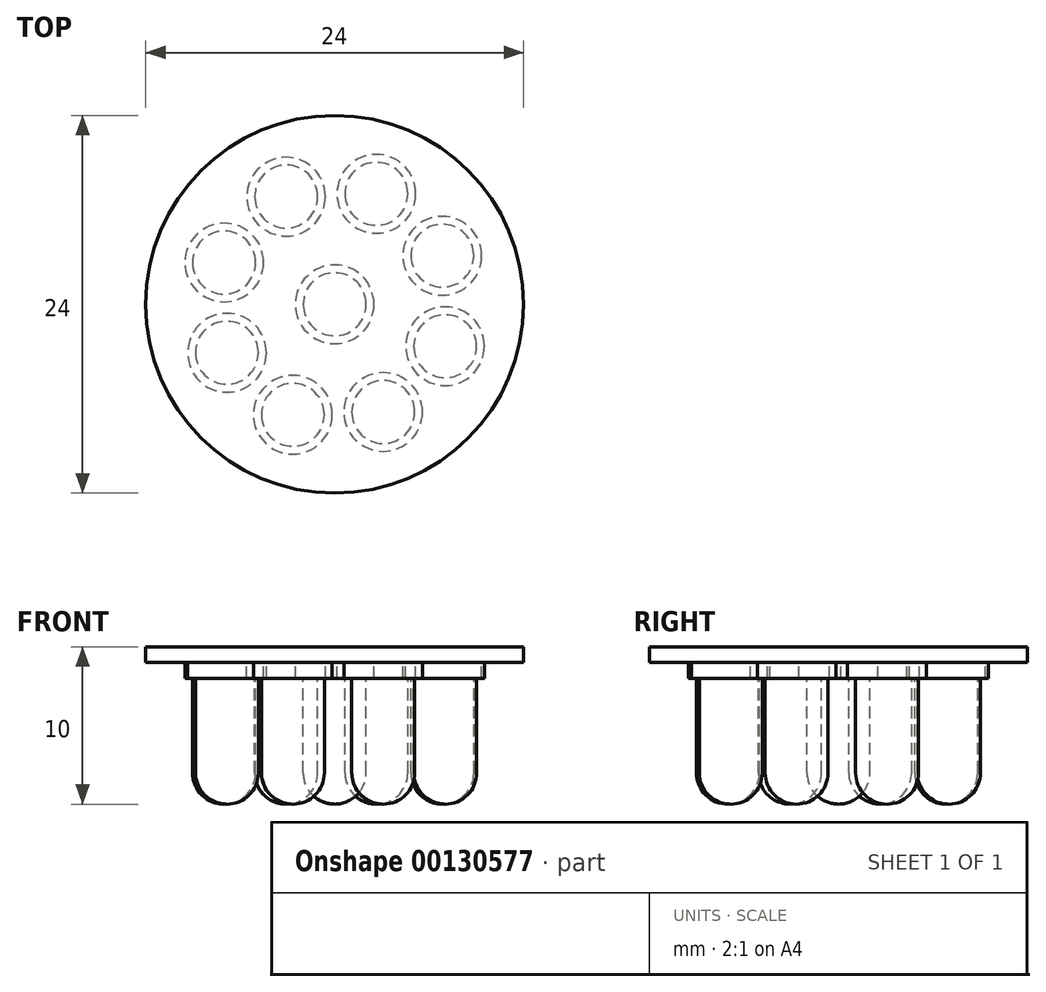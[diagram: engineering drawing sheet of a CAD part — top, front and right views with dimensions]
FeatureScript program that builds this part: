
annotation { "Feature Type Name" : "Feature", "Feature Type Description" : "" }
export const myFeature = defineFeature(function(context is Context, id is Id, definition is map)
    precondition{}
    {
        {
            var Q0;
            Q0=qCreatedBy(makeId("Top.planeOp"),FACE);
            var sketch = newSketch(context, id + "F0", { "sketchPlane" : qUnion([Q0])});
            skCircle(sketch, "E0", {"center": v(0, 0) * mm, "radius": 12 * mm});
            skSolve(sketch);
        }
        {
            var Q0;
            Q0=makeQuery(id+"F0.imprint","IMPRINT",FACE,{"disambiguationData":[TD([[makeQuery(id+"F0.imprint","IMPRINT",EDGE,{"derivedFrom":sQuery(id+"F0.wireOp",EDGE,"E0")}),1.0]])]});
            extrude(context, id + "F1", {"entities" : qUnion([Q0]), "depth" : 1 * mm});
        }
        {
            var Q0;
            Q0=qCreatedBy(makeId("Top.planeOp"),FACE);
            var sketch = newSketch(context, id + "F2", { "sketchPlane" : qUnion([Q0])});
            skCircle(sketch, "E1", {"center": v(0, 0) * mm, "radius": 2.5 * mm});
            skCircle(sketch, "E2", {"center": v(3.08, -6.84) * mm, "radius": 2.5 * mm});
            skCircle(sketch, "E3", {"center": v(7.01, -2.66) * mm, "radius": 2.5 * mm});
            skCircle(sketch, "E4", {"center": v(6.84, 3.08) * mm, "radius": 2.5 * mm});
            skCircle(sketch, "E5", {"center": v(2.65, 7.02) * mm, "radius": 2.5 * mm});
            skCircle(sketch, "E6", {"center": v(-3.09, 6.84) * mm, "radius": 2.5 * mm});
            skCircle(sketch, "E7", {"center": v(-7.01, 2.65) * mm, "radius": 2.5 * mm});
            skCircle(sketch, "E8", {"center": v(-6.84, -3.08) * mm, "radius": 2.5 * mm});
            skCircle(sketch, "E9", {"center": v(-2.66, -7.01) * mm, "radius": 2.5 * mm});
            skSolve(sketch);
        }
        {
            var Q0;
            Q0=makeQuery(id+"F2.imprint","IMPRINT",FACE,{"disambiguationData":[TD([[makeQuery(id+"F2.imprint","IMPRINT",EDGE,{"derivedFrom":sQuery(id+"F2.wireOp",EDGE,"E7")}),1.0]])]});
            var Q1;
            Q1=makeQuery(id+"F2.imprint","IMPRINT",FACE,{"disambiguationData":[TD([[makeQuery(id+"F2.imprint","IMPRINT",EDGE,{"derivedFrom":sQuery(id+"F2.wireOp",EDGE,"E2")}),1.0]])]});
            var Q2;
            Q2=makeQuery(id+"F2.imprint","IMPRINT",FACE,{"disambiguationData":[TD([[makeQuery(id+"F2.imprint","IMPRINT",EDGE,{"derivedFrom":sQuery(id+"F2.wireOp",EDGE,"E6")}),1.0]])]});
            var Q3;
            Q3=makeQuery(id+"F2.imprint","IMPRINT",FACE,{"disambiguationData":[TD([[makeQuery(id+"F2.imprint","IMPRINT",EDGE,{"derivedFrom":sQuery(id+"F2.wireOp",EDGE,"E8")}),1.0]])]});
            var Q4;
            Q4=makeQuery(id+"F2.imprint","IMPRINT",FACE,{"disambiguationData":[TD([[makeQuery(id+"F2.imprint","IMPRINT",EDGE,{"derivedFrom":sQuery(id+"F2.wireOp",EDGE,"E1")}),1.0]])]});
            var Q5;
            Q5=makeQuery(id+"F2.imprint","IMPRINT",FACE,{"disambiguationData":[TD([[makeQuery(id+"F2.imprint","IMPRINT",EDGE,{"derivedFrom":sQuery(id+"F2.wireOp",EDGE,"E4")}),1.0]])]});
            var Q6;
            Q6=makeQuery(id+"F2.imprint","IMPRINT",FACE,{"disambiguationData":[TD([[makeQuery(id+"F2.imprint","IMPRINT",EDGE,{"derivedFrom":sQuery(id+"F2.wireOp",EDGE,"E3")}),1.0]])]});
            var Q7;
            Q7=makeQuery(id+"F2.imprint","IMPRINT",FACE,{"disambiguationData":[TD([[makeQuery(id+"F2.imprint","IMPRINT",EDGE,{"derivedFrom":sQuery(id+"F2.wireOp",EDGE,"E9")}),1.0]])]});
            var Q8;
            Q8=makeQuery(id+"F2.imprint","IMPRINT",FACE,{"disambiguationData":[TD([[makeQuery(id+"F2.imprint","IMPRINT",EDGE,{"derivedFrom":sQuery(id+"F2.wireOp",EDGE,"E5")}),1.0]])]});
            extrude(context, id + "F3", {"entities" : qUnion([Q0, Q1, Q2, Q3, Q4, Q5, Q6, Q7, Q8]), "operationType" : NewBodyOperationType.ADD, "oppositeDirection" : true, "depth" : 1 * mm});
        }
        {
            var Q0;
            Q0=makeQuery(id+"F3.opExtrude","CAP_FACE",FACE,{"disambiguationData":[OSD([sQuery(id+"F2.wireOp",EDGE,"E5")])],"isStart":false});
            var sketch = newSketch(context, id + "F4", { "sketchPlane" : qUnion([Q0])});
            skCircle(sketch, "E10", {"center": v(2.65, -7.02) * mm, "radius": 2 * mm});
            skCircle(sketch, "E11", {"center": v(-3.08, -6.84) * mm, "radius": 2 * mm});
            skCircle(sketch, "E12", {"center": v(-7.02, -2.65) * mm, "radius": 2 * mm});
            skCircle(sketch, "E13", {"center": v(-6.84, 3.08) * mm, "radius": 2 * mm});
            skCircle(sketch, "E14", {"center": v(-2.65, 7.02) * mm, "radius": 2 * mm});
            skCircle(sketch, "E15", {"center": v(3.09, 6.84) * mm, "radius": 2 * mm});
            skCircle(sketch, "E16", {"center": v(7.02, 2.66) * mm, "radius": 2 * mm});
            skCircle(sketch, "E17", {"center": v(6.84, -3.09) * mm, "radius": 2 * mm});
            skCircle(sketch, "E18", {"center": v(0, 0) * mm, "radius": 2 * mm});
            skSolve(sketch);
        }
        {
            var Q0;
            Q0=makeQuery(id+"F4.imprint","IMPRINT",FACE,{"disambiguationData":[TD([[makeQuery(id+"F4.imprint","IMPRINT",EDGE,{"derivedFrom":sQuery(id+"F4.wireOp",EDGE,"E11")}),1.0]])]});
            var Q1;
            Q1=makeQuery(id+"F4.imprint","IMPRINT",FACE,{"disambiguationData":[TD([[makeQuery(id+"F4.imprint","IMPRINT",EDGE,{"derivedFrom":sQuery(id+"F4.wireOp",EDGE,"E17")}),1.0]])]});
            var Q2;
            Q2=makeQuery(id+"F4.imprint","IMPRINT",FACE,{"disambiguationData":[TD([[makeQuery(id+"F4.imprint","IMPRINT",EDGE,{"derivedFrom":sQuery(id+"F4.wireOp",EDGE,"E18")}),1.0]])]});
            var Q3;
            Q3=makeQuery(id+"F4.imprint","IMPRINT",FACE,{"disambiguationData":[TD([[makeQuery(id+"F4.imprint","IMPRINT",EDGE,{"derivedFrom":sQuery(id+"F4.wireOp",EDGE,"E10")}),1.0]])]});
            var Q4;
            Q4=makeQuery(id+"F4.imprint","IMPRINT",FACE,{"disambiguationData":[TD([[makeQuery(id+"F4.imprint","IMPRINT",EDGE,{"derivedFrom":sQuery(id+"F4.wireOp",EDGE,"E14")}),1.0]])]});
            var Q5;
            Q5=makeQuery(id+"F4.imprint","IMPRINT",FACE,{"disambiguationData":[TD([[makeQuery(id+"F4.imprint","IMPRINT",EDGE,{"derivedFrom":sQuery(id+"F4.wireOp",EDGE,"E12")}),1.0]])]});
            var Q6;
            Q6=makeQuery(id+"F4.imprint","IMPRINT",FACE,{"disambiguationData":[TD([[makeQuery(id+"F4.imprint","IMPRINT",EDGE,{"derivedFrom":sQuery(id+"F4.wireOp",EDGE,"E15")}),1.0]])]});
            var Q7;
            Q7=makeQuery(id+"F4.imprint","IMPRINT",FACE,{"disambiguationData":[TD([[makeQuery(id+"F4.imprint","IMPRINT",EDGE,{"derivedFrom":sQuery(id+"F4.wireOp",EDGE,"E16")}),1.0]])]});
            var Q8;
            Q8=makeQuery(id+"F4.imprint","IMPRINT",FACE,{"disambiguationData":[TD([[makeQuery(id+"F4.imprint","IMPRINT",EDGE,{"derivedFrom":sQuery(id+"F4.wireOp",EDGE,"E13")}),1.0]])]});
            extrude(context, id + "F5", {"entities" : qUnion([Q0, Q1, Q2, Q3, Q4, Q5, Q6, Q7, Q8]), "operationType" : NewBodyOperationType.ADD, "depth" : 8 * mm});
        }
        {
            var Q0;
            Q0=makeQuery(id+"F5.opExtrude","CAP_EDGE",EDGE,{"disambiguationData":[OSD([sQuery(id+"F4.wireOp",EDGE,"E18")])],"isStart":false});
            var Q1;
            Q1=makeQuery(id+"F5.opExtrude","CAP_EDGE",EDGE,{"disambiguationData":[OSD([sQuery(id+"F4.wireOp",EDGE,"E14")])],"isStart":false});
            var Q2;
            Q2=makeQuery(id+"F5.opExtrude","CAP_EDGE",EDGE,{"disambiguationData":[OSD([sQuery(id+"F4.wireOp",EDGE,"E10")])],"isStart":false});
            var Q3;
            Q3=makeQuery(id+"F5.opExtrude","CAP_EDGE",EDGE,{"disambiguationData":[OSD([sQuery(id+"F4.wireOp",EDGE,"E16")])],"isStart":false});
            var Q4;
            Q4=makeQuery(id+"F5.opExtrude","CAP_EDGE",EDGE,{"disambiguationData":[OSD([sQuery(id+"F4.wireOp",EDGE,"E11")])],"isStart":false});
            var Q5;
            Q5=makeQuery(id+"F5.opExtrude","CAP_EDGE",EDGE,{"disambiguationData":[OSD([sQuery(id+"F4.wireOp",EDGE,"E17")])],"isStart":false});
            var Q6;
            Q6=makeQuery(id+"F5.opExtrude","CAP_EDGE",EDGE,{"disambiguationData":[OSD([sQuery(id+"F4.wireOp",EDGE,"E12")])],"isStart":false});
            var Q7;
            Q7=makeQuery(id+"F5.opExtrude","CAP_EDGE",EDGE,{"disambiguationData":[OSD([sQuery(id+"F4.wireOp",EDGE,"E15")])],"isStart":false});
            var Q8;
            Q8=makeQuery(id+"F5.opExtrude","CAP_EDGE",EDGE,{"disambiguationData":[OSD([sQuery(id+"F4.wireOp",EDGE,"E13")])],"isStart":false});
            var Q9;
            Q9=makeQuery(id+"F5.opExtrude","CAP_FACE",FACE,{"disambiguationData":[OSD([sQuery(id+"F4.wireOp",EDGE,"E11")])],"isStart":false});
            fillet(context, id + "F6", {"entities" : qUnion([Q0, Q1, Q2, Q3, Q4, Q5, Q6, Q7, Q8, Q9]), "radius" : 2 * mm, "tangentPropagation" : true, "allowEdgeOverflow" : false});
        }
    });
